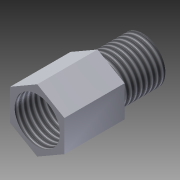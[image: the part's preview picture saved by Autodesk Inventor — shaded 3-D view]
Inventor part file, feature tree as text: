
AUTODESK INVENTOR PART (.ipt)
format: ipt  version: 2015 (Build 190159000, 159)  size: 102,400 bytes
history: native  units: mm
features: extrude x3, sketch x3, thread x2
ambient origin geometry x8: Origin, YZ Plane, XZ Plane, XY Plane, X Axis, Y Axis, Z Axis, Center Point
bodies: Solid1 (feature_tree)
feature tree (8):
  extrude  "Extrusion1"  Depth=3.0mm
  extrude  "Extrusion2"  Depth=10.0mm TaperAngle=0.0deg
  thread  "Thread1"  [1 undecoded]
  extrude  "Extrusion3"  Depth=10.0mm TaperAngle=0.0deg
  thread  "Thread2"  [1 undecoded]
  sketch  "Sketch1"  dims[d1=4.0mm d2=0.0mm d3=3.0mm]
  sketch  "Sketch2"  dims[d4=3.0mm d5=0.0mm d6=10.0mm d7=0.0mm d8=3.0mm]
  sketch  "Sketch3"  dims[d9=3.0mm d10=0.0mm d11=10.0mm d12=0.0mm]
note: 2 required parameter values undecoded (feature->parameter linkage not recoverable at this tier; creation-order binding heuristic only, values carry confidence <= 0.55)
